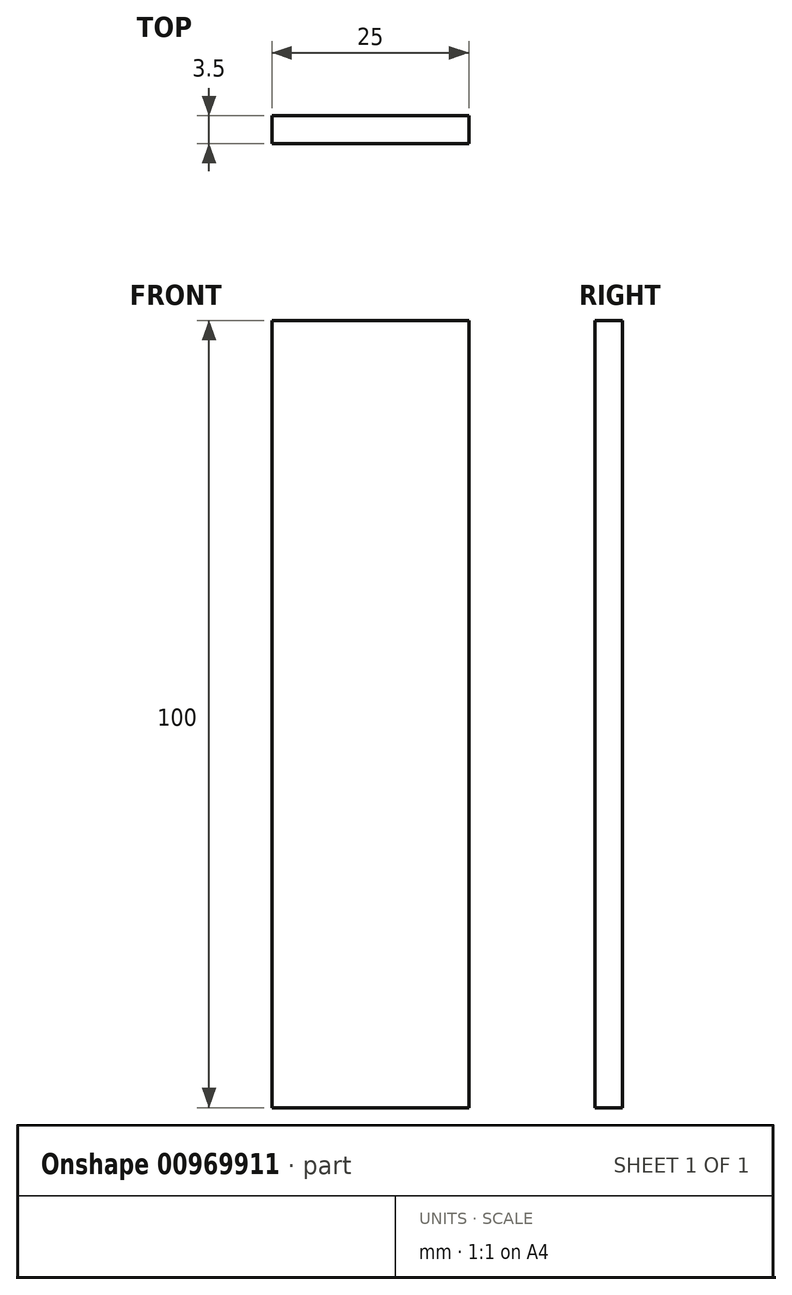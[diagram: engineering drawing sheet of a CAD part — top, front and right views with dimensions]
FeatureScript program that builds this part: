
annotation { "Feature Type Name" : "Feature", "Feature Type Description" : "" }
export const myFeature = defineFeature(function(context is Context, id is Id, definition is map)
    precondition{}
    {
        {
            var Q0;
            Q0=qCreatedBy(makeId("Front.planeOp"),FACE);
            var sketch = newSketch(context, id + "F0", { "sketchPlane" : qUnion([Q0])});
            skLineSegment(sketch, "E0.bottom", {"start": v(-16.69, 61.48) * mm, "end": v(8.31, 61.48) * mm});
            skLineSegment(sketch, "E0.top", {"start": v(-16.69, -38.52) * mm, "end": v(8.31, -38.52) * mm});
            skLineSegment(sketch, "E0.left", {"start": v(-16.69, 61.48) * mm, "end": v(-16.69, -38.52) * mm});
            skLineSegment(sketch, "E0.right", {"start": v(8.31, 61.48) * mm, "end": v(8.31, -38.52) * mm});
            skPoint(sketch, "E1", {"position": v(-4.19, 11.48) * mm});
            skPoint(sketch, "E2", {"position": v(-5.5, 51.48) * mm});
            skPoint(sketch, "E3", {"position": v(-5.68, 33.48) * mm});
            skPoint(sketch, "E4", {"position": v(-5.68, -10.52) * mm});
            skPoint(sketch, "E5", {"position": v(-5.68, -28.52) * mm});
            skLineSegment(sketch, "E6", {"start": v(39.75, 12) * mm, "end": v(8.31, -28.4) * mm});
            skLineSegment(sketch, "E7", {"start": v(8.31, -28.4) * mm, "end": v(39.75, 12) * mm});
            skLineSegment(sketch, "E8", {"start": v(39.75, 12) * mm, "end": v(8.31, 51.48) * mm});
            skLineSegment(sketch, "E9.bottom", {"start": v(-4.19, 11.48) * mm, "end": v(-4.19, 11.48) * mm});
            skSolve(sketch);
        }
        {
            var Q0;
            {var subQ1=sQuery(id+"F0.wireOp",EDGE,"E0.bottom");Q0=makeQuery(id+"F0.imprint","IMPRINT",FACE,{"disambiguationData":[TD([[makeQuery(id+"F0.imprint","IMPRINT",EDGE,{"derivedFrom":subQ1}),-1.0]])]});}
            var Q1;
            {var subQ0=sQuery(id+"F0.wireOp",EDGE,"E7");Q1=makeQuery(id+"F0.imprint","IMPRINT",FACE,{"disambiguationData":[TD([[makeQuery(id+"F0.imprint","IMPRINT",EDGE,{"derivedFrom":subQ0}),1.0]])]});}
            extrude(context, id + "F1", {"entities" : qUnion([Q0, Q1]), "depth" : 3.5 * mm, "offsetDistance" : 25 * mm});
        }
    });
